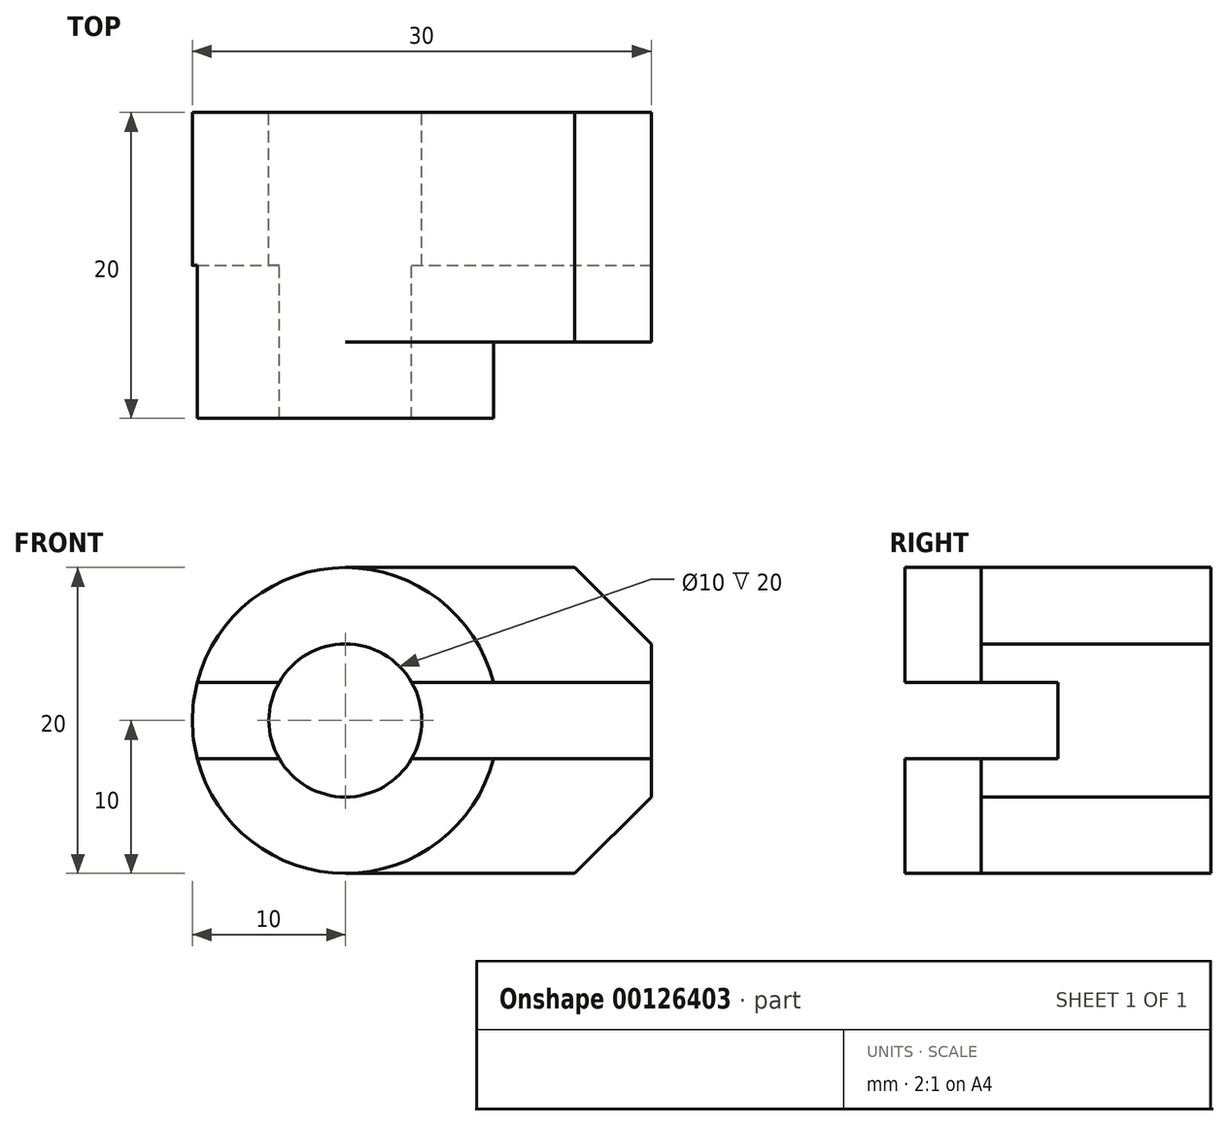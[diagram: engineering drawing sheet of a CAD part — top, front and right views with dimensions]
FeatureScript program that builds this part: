
annotation { "Feature Type Name" : "Feature", "Feature Type Description" : "" }
export const myFeature = defineFeature(function(context is Context, id is Id, definition is map)
    precondition{}
    {
        {
            var Q0;
            Q0=qCreatedBy(makeId("Front.planeOp"),FACE);
            var sketch = newSketch(context, id + "F0", { "sketchPlane" : qUnion([Q0])});
            skCircle(sketch, "E0", {"center": v(0, 0) * mm, "radius": 5 * mm});
            skCircle(sketch, "E1", {"center": v(0, 0) * mm, "radius": 10 * mm});
            skLineSegment(sketch, "E2", {"start": v(0, 10) * mm, "end": v(15, 10) * mm});
            skLineSegment(sketch, "E3", {"start": v(0, -10) * mm, "end": v(15, -10) * mm});
            skLineSegment(sketch, "E4", {"start": v(15, 10) * mm, "end": v(20, 5) * mm});
            skLineSegment(sketch, "E5", {"start": v(20, -5) * mm, "end": v(15, -10) * mm});
            skLineSegment(sketch, "E6", {"start": v(20, 5) * mm, "end": v(20, 0) * mm});
            skLineSegment(sketch, "E7", {"start": v(20, 0) * mm, "end": v(20, -5) * mm});
            skSolve(sketch);
        }
        {
            var Q0;
            Q0=makeQuery(id+"F0.imprint","IMPRINT",FACE,{"disambiguationData":[TD([[makeQuery(id+"F0.imprint","IMPRINT",EDGE,{"derivedFrom":sQuery(id+"F0.wireOp",EDGE,"E0")}),-1.0]])]});
            extrude(context, id + "F1", {"entities" : qUnion([Q0]), "depth" : 20 * mm});
        }
        {
            var Q0;
            {var subQ1=sQuery(id+"F0.wireOp",EDGE,"E2");Q0=makeQuery(id+"F0.imprint","IMPRINT",FACE,{"disambiguationData":[TD([[makeQuery(id+"F0.imprint","IMPRINT",EDGE,{"derivedFrom":subQ1}),-1.0]])]});}
            extrude(context, id + "F2", {"entities" : qUnion([Q0]), "operationType" : NewBodyOperationType.ADD, "depth" : 15 * mm});
        }
        {
            var Q0;
            Q0=makeQuery(id+"F2.opExtrude","SWEPT_FACE",FACE,{"disambiguationData":[OSD([sQuery(id+"F0.wireOp",EDGE,"E6"),sQuery(id+"F0.wireOp",EDGE,"E7")])]});
            var sketch = newSketch(context, id + "F3", { "sketchPlane" : qUnion([Q0])});
            skLineSegment(sketch, "E8.bottom", {"start": v(-10, 2.5) * mm, "end": v(-20, 2.5) * mm});
            skLineSegment(sketch, "E8.top", {"start": v(-10, -2.5) * mm, "end": v(-20, -2.5) * mm});
            skLineSegment(sketch, "E8.left", {"start": v(-10, 2.5) * mm, "end": v(-10, -2.5) * mm});
            skLineSegment(sketch, "E8.right", {"start": v(-20, 2.5) * mm, "end": v(-20, -2.5) * mm});
            skPoint(sketch, "E8.middle", {"position": v(-15, 0) * mm});
            skPoint(sketch, "E8.middle.positionSnap0", {"position": v(-15, 0) * mm});
            skPoint(sketch, "E8.centerSnap0", {"position": v(-15, 0) * mm});
            skSolve(sketch);
        }
        {
            var Q0;
            Q0 = qSketchRegion(id + "F3", true);
            extrude(context, id + "F4", {"entities" : qUnion([Q0]), "operationType" : NewBodyOperationType.REMOVE, "endBound" : BoundingType.THROUGH_ALL, "oppositeDirection" : true, "depth" : 25 * mm});
        }
    });
